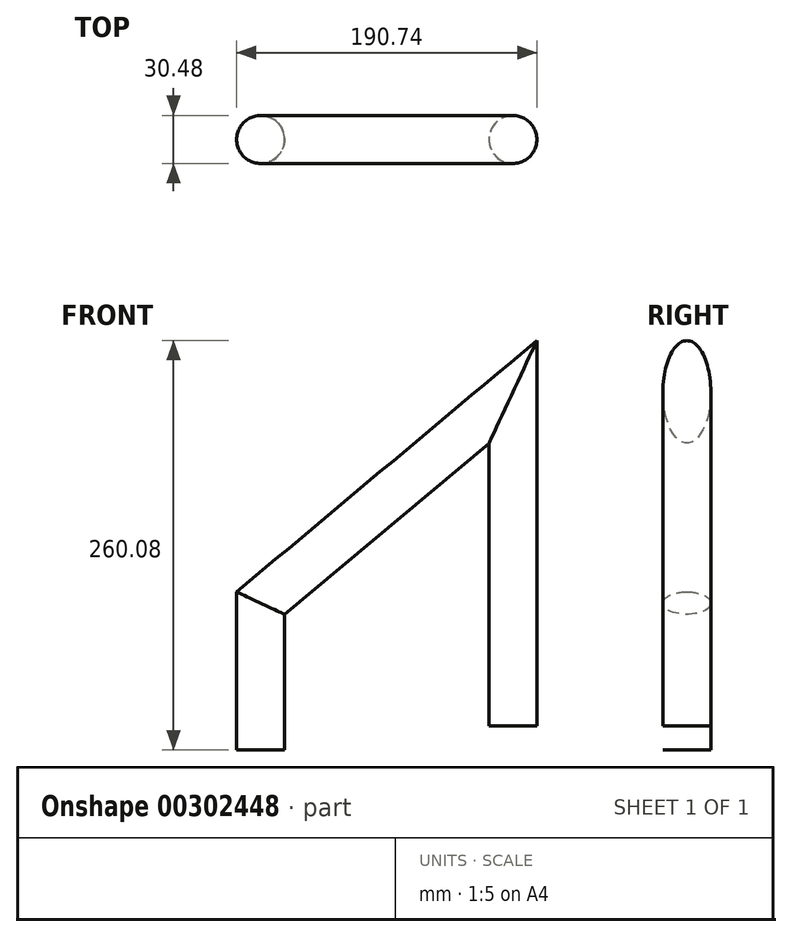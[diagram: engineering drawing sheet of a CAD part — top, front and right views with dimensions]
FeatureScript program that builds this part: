
annotation { "Feature Type Name" : "Feature", "Feature Type Description" : "" }
export const myFeature = defineFeature(function(context is Context, id is Id, definition is map)
    precondition{}
    {
        {
            var Q0;
            Q0=qCreatedBy(makeId("Top.planeOp"),FACE);
            var sketch = newSketch(context, id + "F0", { "sketchPlane" : qUnion([Q0])});
            skCircle(sketch, "E0", {"center": v(0, 0) * mm, "radius": 15.24 * mm});
            skSolve(sketch);
        }
        {
            var Q0;
            Q0=qCreatedBy(makeId("Front.planeOp"),FACE);
            var sketch = newSketch(context, id + "F1", { "sketchPlane" : qUnion([Q0])});
            skLineSegment(sketch, "E1", {"start": v(0, 0) * mm, "end": v(0, 212.02) * mm});
            skLineSegment(sketch, "E2", {"start": v(0, 212.02) * mm, "end": v(-160.26, 77.87) * mm});
            skLineSegment(sketch, "E3", {"start": v(-160.26, 77.87) * mm, "end": v(-160.26, -15.43) * mm});
            skSolve(sketch);
        }
        {
            var Q0;
            Q0=makeQuery(id+"F0.imprint","IMPRINT",FACE,{"disambiguationData":[TD([[makeQuery(id+"F0.imprint","IMPRINT",EDGE,{"derivedFrom":sQuery(id+"F0.wireOp",EDGE,"E0")}),1.0]])]});
            var Q1;
            Q1=sQuery(id+"F1.wireOp",EDGE,"E1");
            var Q2;
            Q2=sQuery(id+"F1.wireOp",EDGE,"E2");
            var Q3;
            Q3=sQuery(id+"F1.wireOp",EDGE,"E3");
            sweep(context, id + "F2", {"profiles" : qUnion([Q0]), "path" : qUnion([Q1, Q2, Q3])});
        }
    });
